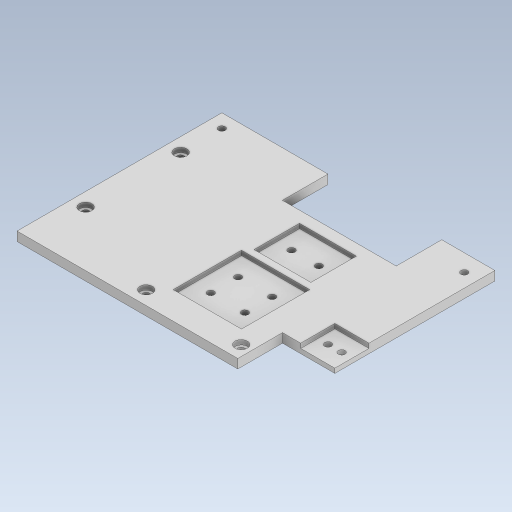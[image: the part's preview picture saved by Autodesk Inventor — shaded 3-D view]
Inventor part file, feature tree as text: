
AUTODESK INVENTOR PART (.ipt)
format: ipt  version: 2023.5 (Build 275446000, 446)  size: 384,512 bytes
history: native  units: in
note: dims shown in document units (in); Inventor stores cm internally (conversion verified against a paired STEP export)
features: extrude x2, sketch x1
ambient origin geometry x8: Origin, YZ Plane, XZ Plane, XY Plane, X Axis, Y Axis, Z Axis, Center Point
bodies: Solid1 (feature_tree)
feature tree (3):
  sketch  "Sketch1"  dims[d0=0.1575in d1=0.0in d2=0.0787in d3=0.0in d4=0.4724in d5=0.2953in d6=0.4724in d7=0.3543in d8=0.0in d10=0.0in d12=0.315in d13=0.2165in d14=0.2165in d15=0.2165in d16=0.2165in]
  extrude  "Extrusion1"  Depth=0.0787in TaperAngle=0.0deg
  extrude  "Extrusion2"  Depth=0.4724in
